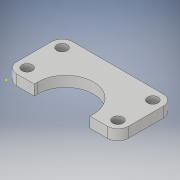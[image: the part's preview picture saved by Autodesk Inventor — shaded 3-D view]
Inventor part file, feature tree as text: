
AUTODESK INVENTOR PART (.ipt)
format: ipt  version: 2018 (Build 220112000, 112)  size: 140,288 bytes
history: native  units: in
note: dims shown in document units (in); Inventor stores cm internally (conversion verified against a paired STEP export)
features: sketch x5, fillet x4, extrude x2, hole x2
ambient origin geometry x8: Origin, YZ Plane, XZ Plane, XY Plane, X Axis, Y Axis, Z Axis, Center Point
bodies: 实体1 (feature_tree)
feature tree (13):
  sketch  "草图1"  dims[d0=6.2992in d1=3.1496in d2=0.5906in d3=0.0in d4=0.5906in d5=0.5906in d6=0.5906in]
  extrude  "拉伸1"  Depth=3.1496in
  fillet  "圆角1"  Radius=0.5906in
  fillet  "圆角2"  Radius=0.5906in
  fillet  "圆角3"  Radius=0.5906in
  fillet  "圆角4"  Radius=0.5906in
  hole  "孔1"  [1 undecoded]
  extrude  "拉伸2"  [1 undecoded]
  hole  "孔2"  [1 undecoded]
  sketch  "草图2"  dims[d7=0.5906in]
  sketch  "草图4"  dims[d8=0.5906in d9=0.2362in d10=0.1575in d11=0.0787in d12=90.0deg d13=0.315in d14=0.8108in d19=0.5906in d20=0.0in]
  sketch  "草图5"  dims[d21=3.1496in d22=0.2362in d23=0.1575in d24=0.0787in d25=90.0deg d26=0.315in d27=0.8108in]
  sketch  "草图6"
note: 3 required parameter values undecoded (feature->parameter linkage not recoverable at this tier; creation-order binding heuristic only, values carry confidence <= 0.55)
